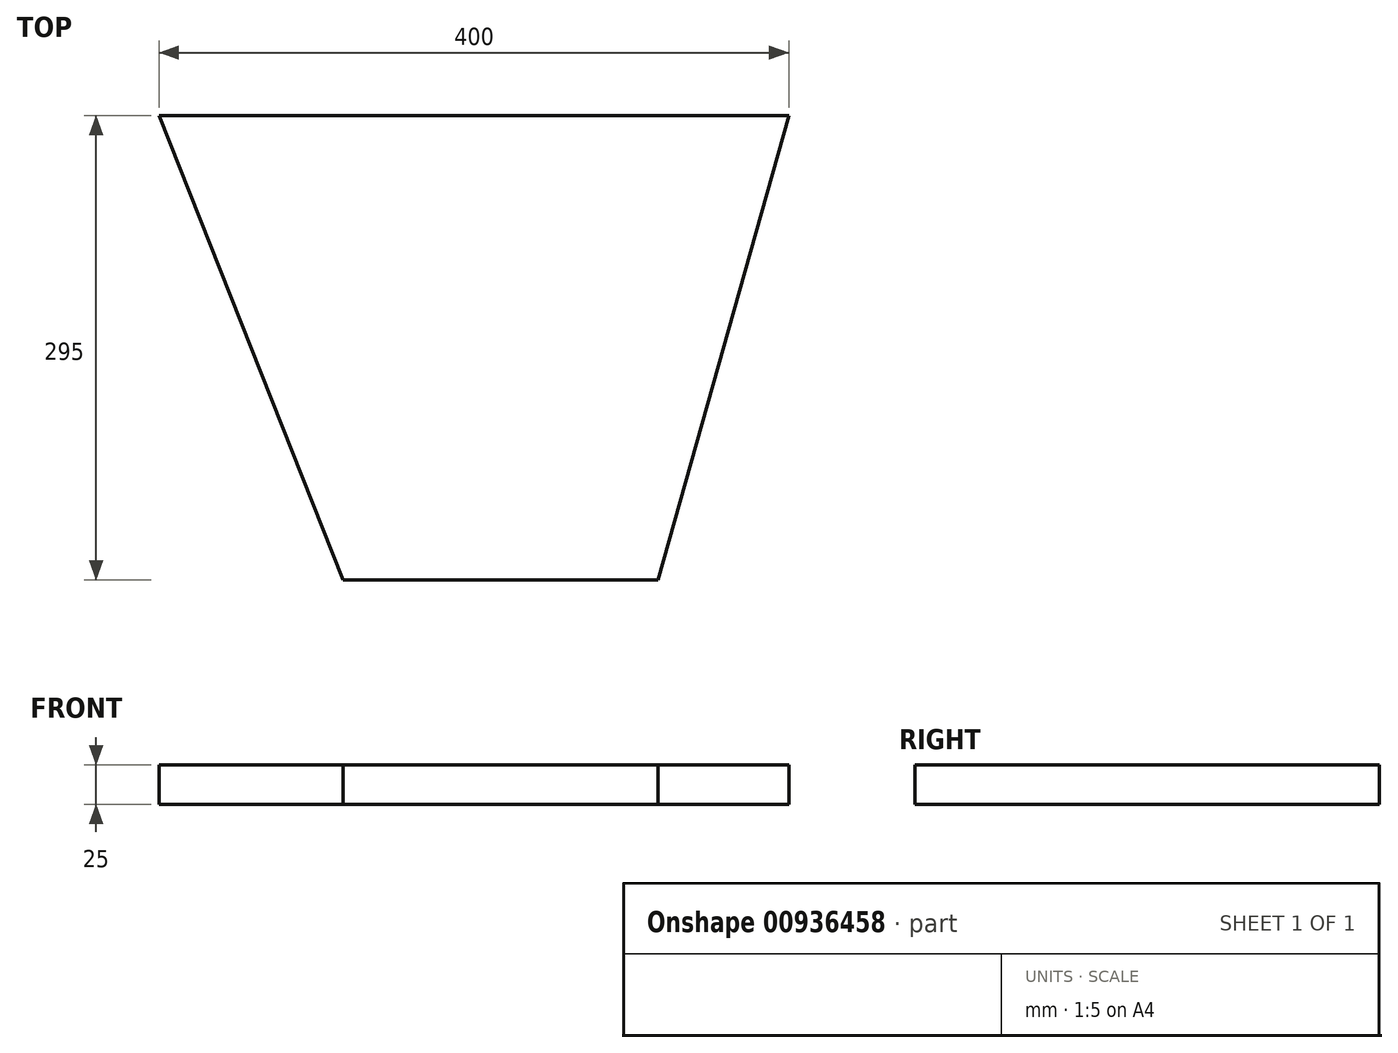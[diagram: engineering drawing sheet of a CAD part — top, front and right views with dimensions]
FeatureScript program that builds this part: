
annotation { "Feature Type Name" : "Feature", "Feature Type Description" : "" }
export const myFeature = defineFeature(function(context is Context, id is Id, definition is map)
    precondition{}
    {
        {
            var Q0;
            Q0=qCreatedBy(makeId("Top.planeOp"),FACE);
            var sketch = newSketch(context, id + "F0", { "sketchPlane" : qUnion([Q0])});
            skLineSegment(sketch, "E0.bottom", {"start": v(-135.12, 90.83) * mm, "end": v(264.88, 90.83) * mm});
            skLineSegment(sketch, "E0.top", {"start": v(-18.14, -204.17) * mm, "end": v(181.86, -204.17) * mm});
            skLineSegment(sketch, "E1", {"start": v(-135.12, 90.83) * mm, "end": v(-18.14, -204.17) * mm});
            skLineSegment(sketch, "E2", {"start": v(264.88, 90.83) * mm, "end": v(181.86, -204.17) * mm});
            skSolve(sketch);
        }
        {
            var Q0;
            Q0 = qSketchRegion(id + "F0", true);
            extrude(context, id + "F1", {"entities" : qUnion([Q0]), "depth" : 25 * mm, "offsetDistance" : 25 * mm});
        }
        {
            var Q0;
            Q0 = qSketchRegion(id + "F0", true);
            extrude(context, id + "F2", {"entities" : qUnion([Q0]), "operationType" : NewBodyOperationType.ADD, "depth" : 25 * mm, "offsetDistance" : 25 * mm});
        }
        {
            var Q0;
            Q0 = qSketchRegion(id + "F0", true);
            extrude(context, id + "F3", {"entities" : qUnion([Q0]), "operationType" : NewBodyOperationType.ADD, "depth" : 25 * mm, "offsetDistance" : 25 * mm});
        }
        {
            var Q0;
            Q0 = qSketchRegion(id + "F0", true);
            extrude(context, id + "F4", {"entities" : qUnion([Q0]), "operationType" : NewBodyOperationType.ADD, "depth" : 25 * mm, "offsetDistance" : 25 * mm});
        }
        {
            var Q0;
            Q0 = qSketchRegion(id + "F0", true);
            extrude(context, id + "F5", {"entities" : qUnion([Q0]), "operationType" : NewBodyOperationType.ADD, "depth" : 25 * mm, "offsetDistance" : 25 * mm});
        }
        {
            var Q0;
            Q0 = qSketchRegion(id + "F0", true);
            extrude(context, id + "F6", {"entities" : qUnion([Q0]), "operationType" : NewBodyOperationType.ADD, "depth" : 25 * mm, "offsetDistance" : 25 * mm});
        }
    });
